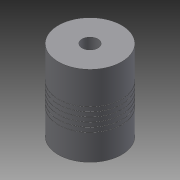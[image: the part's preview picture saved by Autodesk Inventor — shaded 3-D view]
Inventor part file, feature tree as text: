
AUTODESK INVENTOR PART (.ipt)
format: ipt  version: 2015 (Build 190159000, 159)  size: 131,584 bytes
history: native  units: in
note: dims shown in document units (in); Inventor stores cm internally (conversion verified against a paired STEP export)
features: revolve x1, sketch x1
ambient origin geometry x8: Origin, YZ Plane, XZ Plane, XY Plane, X Axis, Y Axis, Z Axis, Center Point
bodies: Body1 (feature_tree)
feature tree (2):
  revolve  "Revolution2"  [1 undecoded]
  sketch  "Sketch2"  dims[d1=0.2in d2=0.2in d3=1.0in d4=0.005in d5=0.005in d6=0.005in d7=0.005in d8=0.005in d10=0.005in d12=0.05in d13=0.05in d14=0.05in d15=0.05in d16=0.05in d17=0.0984in d18=0.1969in d20=0.3937in d21=0.2in d22=90.0deg]
note: 1 required parameter value undecoded (feature->parameter linkage not recoverable at this tier; creation-order binding heuristic only, values carry confidence <= 0.55)
